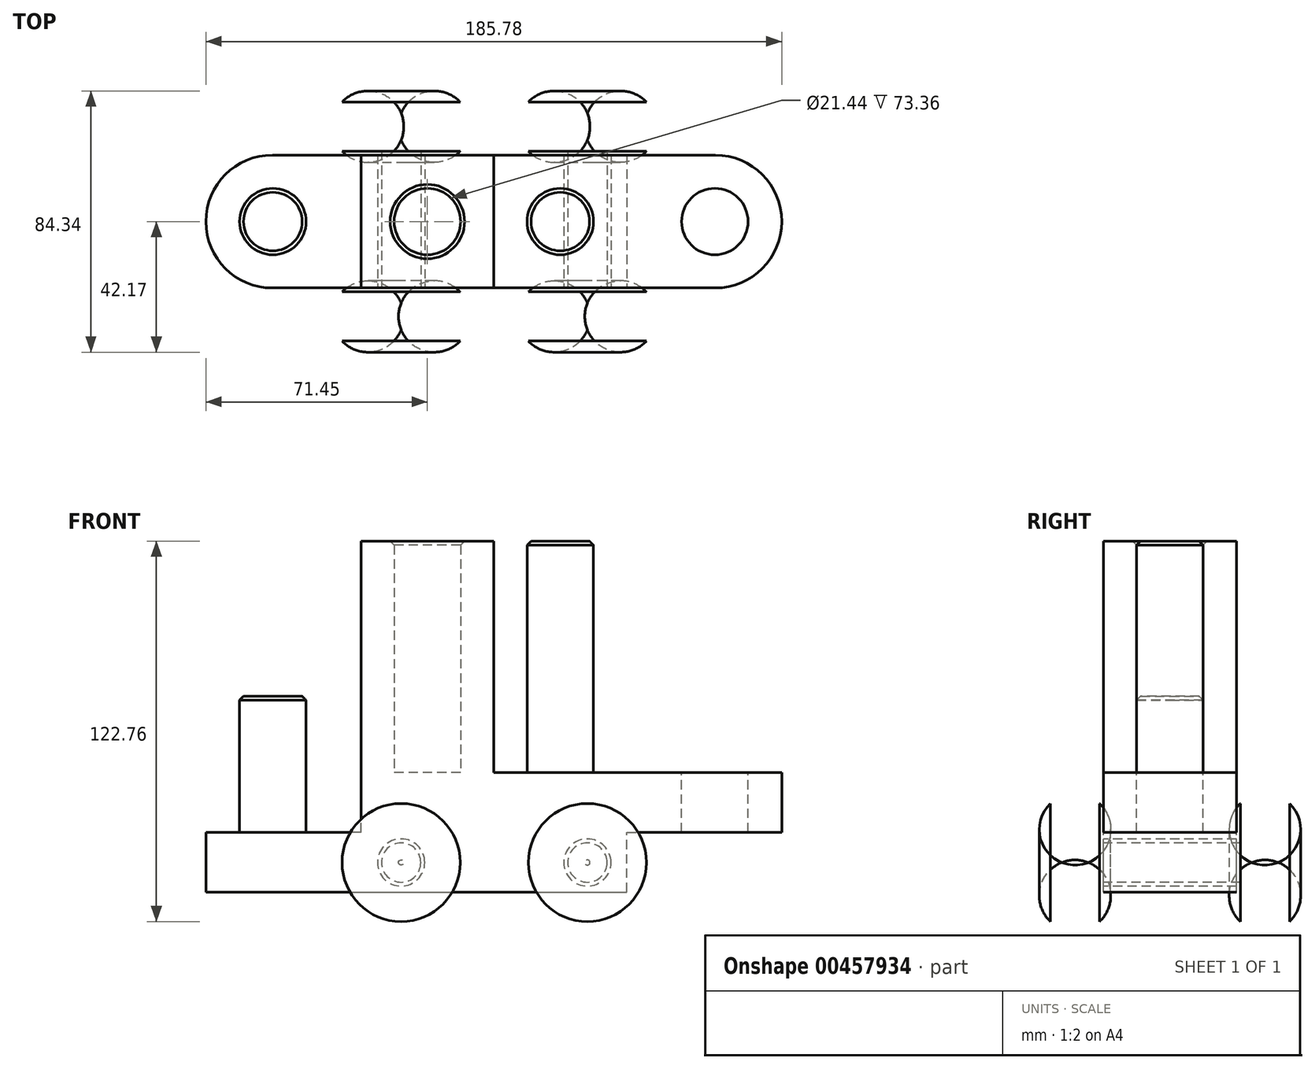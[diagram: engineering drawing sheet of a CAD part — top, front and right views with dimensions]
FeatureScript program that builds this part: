
annotation { "Feature Type Name" : "Feature", "Feature Type Description" : "" }
export const myFeature = defineFeature(function(context is Context, id is Id, definition is map)
    precondition{}
    {
        {
            var Q0;
            Q0=qCreatedBy(makeId("Top.planeOp"),FACE);
            var sketch = newSketch(context, id + "F0", { "sketchPlane" : qUnion([Q0])});
            skLineSegment(sketch, "E0.bottom", {"start": v(-42.88, 21.44) * mm, "end": v(42.88, 21.44) * mm});
            skLineSegment(sketch, "E0.top", {"start": v(-42.88, -21.44) * mm, "end": v(42.88, -21.44) * mm});
            skLineSegment(sketch, "E0.left", {"start": v(-42.88, 21.44) * mm, "end": v(-42.88, -21.44) * mm});
            skLineSegment(sketch, "E0.right", {"start": v(42.88, 21.44) * mm, "end": v(42.88, -21.44) * mm});
            skPoint(sketch, "E0.middle", {"position": v(0, 0) * mm});
            skLineSegment(sketch, "E1", {"start": v(-42.88, 0) * mm, "end": v(0, 0) * mm});
            skLineSegment(sketch, "E2", {"start": v(42.88, 0) * mm, "end": v(0, 0) * mm});
            skPoint(sketch, "E3", {"position": v(-21.44, 0) * mm});
            skPoint(sketch, "E4", {"position": v(21.44, 0) * mm});
            skCircle(sketch, "E5", {"center": v(-21.44, 0) * mm, "radius": 10.72 * mm});
            skCircle(sketch, "E6", {"center": v(21.44, 0) * mm, "radius": 10.72 * mm});
            skLineSegment(sketch, "E7", {"start": v(42.88, 21.44) * mm, "end": v(71.45, 21.44) * mm});
            skLineSegment(sketch, "E8", {"start": v(42.88, -21.44) * mm, "end": v(71.45, -21.44) * mm});
            skArc(sketch, "E9", {"start": v(71.45, -21.44) * mm, "mid": v(92.89, 0) * mm, "end": v(71.45, 21.44) * mm});
            skLineSegment(sketch, "E10", {"start": v(42.88, 0) * mm, "end": v(92.89, 0) * mm});
            skPoint(sketch, "E11", {"position": v(82.02, 0) * mm});
            skCircle(sketch, "E12", {"center": v(71.3, 0) * mm, "radius": 10.72 * mm});
            skLineSegment(sketch, "E13", {"start": v(0, 21.44) * mm, "end": v(0, -21.44) * mm});
            skLineSegment(sketch, "E14.MirrorCS", {"start": v(-42.88, 21.44) * mm, "end": v(-71.45, 21.44) * mm});
            skCircle(sketch, "E15.MirrorC", {"center": v(-71.3, 0) * mm, "radius": 10.72 * mm});
            skLineSegment(sketch, "E16.MirrorCS", {"start": v(-42.88, -21.44) * mm, "end": v(-71.45, -21.44) * mm});
            skPoint(sketch, "E17.MirrorP", {"position": v(-82.02, 0) * mm});
            skLineSegment(sketch, "E18.MirrorCS", {"start": v(-42.88, 0) * mm, "end": v(-92.89, 0) * mm});
            skArc(sketch, "E19.MirrorCS", {"start": v(-71.45, -21.44) * mm, "mid": v(-92.89, 0) * mm, "end": v(-71.45, 21.44) * mm});
            skSolve(sketch);
        }
        {
            var Q0;
            {var subQ6=sQuery(id+"F0.wireOp",EDGE,"E0.bottom");Q0=makeQuery(id+"F0.imprint","IMPRINT",FACE,{"disambiguationData":[TD([[makeQuery(id+"F0.imprint","IMPRINT",EDGE,{"derivedFrom":subQ6}),-1.0]])]});}
            var Q1;
            {var subQ0=sQuery(id+"F0.wireOp",EDGE,"E5");var subQ1=sQuery(id+"F0.wireOp",EDGE,"E1");var subQ2=makeQuery(id+"F0.imprint","INTERSECT",VERTEX,{"disambiguationData":[OD(0.0)],"derivedFrom":[subQ1,subQ0]});Q1=makeQuery(id+"F0.imprint","IMPRINT",FACE,{"disambiguationData":[TD([[makeQuery(id+"F0.imprint","IMPRINT",EDGE,{"disambiguationData":[TD([[subQ2,-1.0]])],"derivedFrom":subQ1}),1.0]])]});}
            var Q2;
            {var subQ0=sQuery(id+"F0.wireOp",EDGE,"E5");var subQ1=sQuery(id+"F0.wireOp",EDGE,"E1");var subQ2=makeQuery(id+"F0.imprint","INTERSECT",VERTEX,{"disambiguationData":[OD(0.0)],"derivedFrom":[subQ1,subQ0]});Q2=makeQuery(id+"F0.imprint","IMPRINT",FACE,{"disambiguationData":[TD([[makeQuery(id+"F0.imprint","IMPRINT",EDGE,{"disambiguationData":[TD([[subQ2,-1.0]])],"derivedFrom":subQ1}),-1.0]])]});}
            var Q3;
            {var subQ0=sQuery(id+"F0.wireOp",EDGE,"E6");var subQ1=sQuery(id+"F0.wireOp",EDGE,"E2");var subQ2=makeQuery(id+"F0.imprint","INTERSECT",VERTEX,{"disambiguationData":[OD(0.0)],"derivedFrom":[subQ1,subQ0]});Q3=makeQuery(id+"F0.imprint","IMPRINT",FACE,{"disambiguationData":[TD([[makeQuery(id+"F0.imprint","IMPRINT",EDGE,{"disambiguationData":[TD([[subQ2,-1.0]])],"derivedFrom":subQ1}),-1.0]])]});}
            var Q4;
            {var subQ0=sQuery(id+"F0.wireOp",EDGE,"E6");var subQ1=sQuery(id+"F0.wireOp",EDGE,"E2");var subQ2=makeQuery(id+"F0.imprint","INTERSECT",VERTEX,{"disambiguationData":[OD(0.0)],"derivedFrom":[subQ1,subQ0]});Q4=makeQuery(id+"F0.imprint","IMPRINT",FACE,{"disambiguationData":[TD([[makeQuery(id+"F0.imprint","IMPRINT",EDGE,{"disambiguationData":[TD([[subQ2,-1.0]])],"derivedFrom":subQ1}),1.0]])]});}
            var Q5;
            {var subQ1=sQuery(id+"F0.wireOp",EDGE,"E0.top");Q5=makeQuery(id+"F0.imprint","IMPRINT",FACE,{"disambiguationData":[TD([[makeQuery(id+"F0.imprint","IMPRINT",EDGE,{"derivedFrom":subQ1}),1.0]])]});}
            var Q6;
            {var subQ0=sQuery(id+"F0.wireOp",EDGE,"E1");var subQ1=sQuery(id+"F0.wireOp",EDGE,"E5");var subQ2=makeQuery(id+"F0.imprint","INTERSECT",VERTEX,{"disambiguationData":[OD(0.0)],"derivedFrom":[subQ1,subQ0]});Q6=makeQuery(id+"F0.imprint","IMPRINT",FACE,{"disambiguationData":[TD([[makeQuery(id+"F0.imprint","IMPRINT",EDGE,{"disambiguationData":[TD([[subQ2,-1.0]])],"derivedFrom":subQ1}),-1.0]])]});}
            var Q7;
            {var subQ0=sQuery(id+"F0.wireOp",EDGE,"E1");var subQ1=sQuery(id+"F0.wireOp",EDGE,"E5");var subQ2=makeQuery(id+"F0.imprint","INTERSECT",VERTEX,{"disambiguationData":[OD(0.0)],"derivedFrom":[subQ1,subQ0]});Q7=makeQuery(id+"F0.imprint","IMPRINT",FACE,{"disambiguationData":[TD([[makeQuery(id+"F0.imprint","IMPRINT",EDGE,{"disambiguationData":[TD([[subQ2,1.0]])],"derivedFrom":subQ1}),-1.0]])]});}
            extrude(context, id + "F1", {"entities" : qUnion([Q0, Q1, Q2, Q3, Q4, Q5, Q6, Q7]), "oppositeDirection" : true, "depth" : 38.6 * mm, "offsetDistance" : 25.4 * mm});
        }
        {
            var Q0;
            {var subQ0=sQuery(id+"F0.wireOp",EDGE,"E1");var subQ1=sQuery(id+"F0.wireOp",EDGE,"E5");var subQ2=makeQuery(id+"F0.imprint","INTERSECT",VERTEX,{"disambiguationData":[OD(0.0)],"derivedFrom":[subQ1,subQ0]});Q0=makeQuery(id+"F0.imprint","IMPRINT",FACE,{"disambiguationData":[TD([[makeQuery(id+"F0.imprint","IMPRINT",EDGE,{"disambiguationData":[TD([[subQ2,-1.0]])],"derivedFrom":subQ1}),-1.0]])]});}
            var Q1;
            {var subQ0=sQuery(id+"F0.wireOp",EDGE,"E1");var subQ1=sQuery(id+"F0.wireOp",EDGE,"E5");var subQ2=makeQuery(id+"F0.imprint","INTERSECT",VERTEX,{"disambiguationData":[OD(0.0)],"derivedFrom":[subQ1,subQ0]});Q1=makeQuery(id+"F0.imprint","IMPRINT",FACE,{"disambiguationData":[TD([[makeQuery(id+"F0.imprint","IMPRINT",EDGE,{"disambiguationData":[TD([[subQ2,1.0]])],"derivedFrom":subQ1}),-1.0]])]});}
            var Q2;
            {var subQ0=sQuery(id+"F0.wireOp",EDGE,"E6");var subQ1=sQuery(id+"F0.wireOp",EDGE,"E2");var subQ2=makeQuery(id+"F0.imprint","INTERSECT",VERTEX,{"disambiguationData":[OD(0.0)],"derivedFrom":[subQ1,subQ0]});Q2=makeQuery(id+"F0.imprint","IMPRINT",FACE,{"disambiguationData":[TD([[makeQuery(id+"F0.imprint","IMPRINT",EDGE,{"disambiguationData":[TD([[subQ2,-1.0]])],"derivedFrom":subQ1}),-1.0]])]});}
            var Q3;
            {var subQ0=sQuery(id+"F0.wireOp",EDGE,"E6");var subQ1=sQuery(id+"F0.wireOp",EDGE,"E2");var subQ2=makeQuery(id+"F0.imprint","INTERSECT",VERTEX,{"disambiguationData":[OD(0.0)],"derivedFrom":[subQ1,subQ0]});Q3=makeQuery(id+"F0.imprint","IMPRINT",FACE,{"disambiguationData":[TD([[makeQuery(id+"F0.imprint","IMPRINT",EDGE,{"disambiguationData":[TD([[subQ2,-1.0]])],"derivedFrom":subQ1}),1.0]])]});}
            extrude(context, id + "F2", {"entities" : qUnion([Q0, Q1, Q2, Q3]), "operationType" : NewBodyOperationType.ADD, "depth" : 74.63 * mm, "offsetDistance" : 25.4 * mm});
        }
        {
            var Q0;
            {var subQ5=sQuery(id+"F0.wireOp",EDGE,"E7");Q0=makeQuery(id+"F0.imprint","IMPRINT",FACE,{"disambiguationData":[TD([[makeQuery(id+"F0.imprint","IMPRINT",EDGE,{"derivedFrom":subQ5}),-1.0]])]});}
            var Q1;
            {var subQ1=sQuery(id+"F0.wireOp",EDGE,"E8");Q1=makeQuery(id+"F0.imprint","IMPRINT",FACE,{"disambiguationData":[TD([[makeQuery(id+"F0.imprint","IMPRINT",EDGE,{"derivedFrom":subQ1}),1.0]])]});}
            extrude(context, id + "F3", {"entities" : qUnion([Q0, Q1]), "operationType" : NewBodyOperationType.ADD, "oppositeDirection" : true, "depth" : 19.3 * mm, "offsetDistance" : 25.4 * mm});
        }
        {
            var Q0;
            {var subQ8=sQuery(id+"F0.wireOp",EDGE,"E14.MirrorCS");Q0=makeQuery(id+"F0.imprint","IMPRINT",FACE,{"disambiguationData":[TD([[makeQuery(id+"F0.imprint","IMPRINT",EDGE,{"derivedFrom":subQ8}),1.0]])]});}
            var Q1;
            {var subQ5=sQuery(id+"F0.wireOp",EDGE,"E16.MirrorCS");Q1=makeQuery(id+"F0.imprint","IMPRINT",FACE,{"disambiguationData":[TD([[makeQuery(id+"F0.imprint","IMPRINT",EDGE,{"derivedFrom":subQ5}),-1.0]])]});}
            var Q2;
            {var subQ0=sQuery(id+"F0.wireOp",EDGE,"E15.MirrorC");var subQ1=sQuery(id+"F0.wireOp",EDGE,"E18.MirrorCS");var subQ2=makeQuery(id+"F0.imprint","INTERSECT",VERTEX,{"disambiguationData":[OD(0.0)],"derivedFrom":[subQ1,subQ0]});Q2=makeQuery(id+"F0.imprint","IMPRINT",FACE,{"disambiguationData":[TD([[makeQuery(id+"F0.imprint","IMPRINT",EDGE,{"disambiguationData":[TD([[subQ2,-1.0]])],"derivedFrom":subQ1}),-1.0]])]});}
            var Q3;
            {var subQ0=sQuery(id+"F0.wireOp",EDGE,"E15.MirrorC");var subQ1=sQuery(id+"F0.wireOp",EDGE,"E18.MirrorCS");var subQ2=makeQuery(id+"F0.imprint","INTERSECT",VERTEX,{"disambiguationData":[OD(0.0)],"derivedFrom":[subQ1,subQ0]});Q3=makeQuery(id+"F0.imprint","IMPRINT",FACE,{"disambiguationData":[TD([[makeQuery(id+"F0.imprint","IMPRINT",EDGE,{"disambiguationData":[TD([[subQ2,-1.0]])],"derivedFrom":subQ1}),1.0]])]});}
            extrude(context, id + "F4", {"entities" : qUnion([Q0, Q1, Q2, Q3]), "operationType" : NewBodyOperationType.ADD, "oppositeDirection" : true, "depth" : 38.6 * mm, "offsetDistance" : 25.4 * mm});
        }
        {
            var Q0;
            {var subQ8=sQuery(id+"F0.wireOp",EDGE,"E14.MirrorCS");Q0=makeQuery(id+"F0.imprint","IMPRINT",FACE,{"disambiguationData":[TD([[makeQuery(id+"F0.imprint","IMPRINT",EDGE,{"derivedFrom":subQ8}),1.0]])]});}
            var Q1;
            {var subQ5=sQuery(id+"F0.wireOp",EDGE,"E16.MirrorCS");Q1=makeQuery(id+"F0.imprint","IMPRINT",FACE,{"disambiguationData":[TD([[makeQuery(id+"F0.imprint","IMPRINT",EDGE,{"derivedFrom":subQ5}),-1.0]])]});}
            extrude(context, id + "F5", {"entities" : qUnion([Q0, Q1]), "operationType" : NewBodyOperationType.REMOVE, "oppositeDirection" : true, "depth" : 19.3 * mm, "offsetDistance" : 25.4 * mm});
        }
        {
            var Q0;
            {var subQ0=sQuery(id+"F0.wireOp",EDGE,"E15.MirrorC");var subQ1=sQuery(id+"F0.wireOp",EDGE,"E18.MirrorCS");var subQ2=makeQuery(id+"F0.imprint","INTERSECT",VERTEX,{"disambiguationData":[OD(0.0)],"derivedFrom":[subQ1,subQ0]});Q0=makeQuery(id+"F0.imprint","IMPRINT",FACE,{"disambiguationData":[TD([[makeQuery(id+"F0.imprint","IMPRINT",EDGE,{"disambiguationData":[TD([[subQ2,-1.0]])],"derivedFrom":subQ1}),-1.0]])]});}
            var Q1;
            {var subQ0=sQuery(id+"F0.wireOp",EDGE,"E15.MirrorC");var subQ1=sQuery(id+"F0.wireOp",EDGE,"E18.MirrorCS");var subQ2=makeQuery(id+"F0.imprint","INTERSECT",VERTEX,{"disambiguationData":[OD(0.0)],"derivedFrom":[subQ1,subQ0]});Q1=makeQuery(id+"F0.imprint","IMPRINT",FACE,{"disambiguationData":[TD([[makeQuery(id+"F0.imprint","IMPRINT",EDGE,{"disambiguationData":[TD([[subQ2,-1.0]])],"derivedFrom":subQ1}),1.0]])]});}
            extrude(context, id + "F6", {"entities" : qUnion([Q0, Q1]), "operationType" : NewBodyOperationType.ADD, "depth" : 24.59 * mm, "offsetDistance" : 25.4 * mm});
        }
        {
            var Q0;
            Q0=makeQuery(id+"F2.opExtrude","CAP_EDGE",EDGE,{"disambiguationData":[OSD([sQuery(id+"F0.wireOp",EDGE,"E5")])],"isStart":false});
            chamfer(context, id + "F7", {"entities" : qUnion([Q0]), "width" : 1.27 * mm, "tangentPropagation" : true});
        }
        {
            var Q0;
            Q0=makeQuery(id+"F2.opExtrude","CAP_EDGE",EDGE,{"disambiguationData":[OSD([sQuery(id+"F0.wireOp",EDGE,"E6")])],"isStart":false});
            chamfer(context, id + "F8", {"entities" : qUnion([Q0]), "width" : 1.27 * mm, "tangentPropagation" : true});
        }
        {
            var Q0;
            Q0=makeQuery(id+"F6.opExtrude","CAP_EDGE",EDGE,{"disambiguationData":[OSD([sQuery(id+"F0.wireOp",EDGE,"E15.MirrorC")])],"isStart":false});
            chamfer(context, id + "F9", {"entities" : qUnion([Q0]), "width" : 1.27 * mm, "tangentPropagation" : true});
        }
        {
            var Q0;
            Q0=makeQuery(id+"F4.boolean.opBoolean","MERGE",FACE,{"derivedFrom":[makeQuery(id+"F3.boolean.opBoolean","MERGE",FACE,{"derivedFrom":[makeQuery(id+"F1.opExtrude","SWEPT_FACE",FACE,{"disambiguationData":[OSD([sQuery(id+"F0.wireOp",EDGE,"E0.top")])]}),makeQuery(id+"F3.opExtrude","SWEPT_FACE",FACE,{"disambiguationData":[OSD([sQuery(id+"F0.wireOp",EDGE,"E8")])]})]}),makeQuery(id+"F4.opExtrude","SWEPT_FACE",FACE,{"disambiguationData":[OSD([sQuery(id+"F0.wireOp",EDGE,"E16.MirrorCS")])]})]});
            var sketch = newSketch(context, id + "F10", { "sketchPlane" : qUnion([Q0])});
            skPoint(sketch, "E20", {"position": v(42.88, -29.08) * mm});
            skLineSegment(sketch, "E21", {"start": v(42.88, -29.08) * mm, "end": v(30.18, -29.08) * mm});
            skCircle(sketch, "E22", {"center": v(30.18, -29.08) * mm, "radius": 6.35 * mm});
            skCircle(sketch, "E23", {"center": v(30.18, -29.08) * mm, "radius": 7.62 * mm});
            skLineSegment(sketch, "E24", {"start": v(30.18, -29.08) * mm, "end": v(-29.91, -29.08) * mm});
            skCircle(sketch, "E25", {"center": v(-29.91, -29.08) * mm, "radius": 6.35 * mm});
            skCircle(sketch, "E26", {"center": v(-29.91, -29.08) * mm, "radius": 7.62 * mm});
            skSolve(sketch);
        }
        {
            var Q0;
            {var subQ0=sQuery(id+"F10.wireOp",EDGE,"E23");var subQ1=sQuery(id+"F10.wireOp",EDGE,"E21");var subQ2=makeQuery(id+"F10.imprint","INTERSECT",VERTEX,{"derivedFrom":[subQ1,subQ0]});Q0=makeQuery(id+"F10.imprint","IMPRINT",FACE,{"disambiguationData":[TD([[makeQuery(id+"F10.imprint","IMPRINT",EDGE,{"disambiguationData":[TD([[subQ2,-1.0]])],"derivedFrom":subQ1}),-1.0]])]});}
            var Q1;
            {var subQ0=sQuery(id+"F10.wireOp",EDGE,"E23");var subQ1=sQuery(id+"F10.wireOp",EDGE,"E21");var subQ2=makeQuery(id+"F10.imprint","INTERSECT",VERTEX,{"derivedFrom":[subQ1,subQ0]});Q1=makeQuery(id+"F10.imprint","IMPRINT",FACE,{"disambiguationData":[TD([[makeQuery(id+"F10.imprint","IMPRINT",EDGE,{"disambiguationData":[TD([[subQ2,-1.0]])],"derivedFrom":subQ1}),1.0]])]});}
            var Q2;
            Q2=makeQuery(id+"F10.imprint","IMPRINT",FACE,{"disambiguationData":[TD([[makeQuery(id+"F10.imprint","IMPRINT",EDGE,{"derivedFrom":sQuery(id+"F10.wireOp",EDGE,"E25")}),-1.0]])]});
            var Q3;
            Q3=makeQuery(id+"F4.boolean.opBoolean","MERGE",FACE,{"derivedFrom":[makeQuery(id+"F3.boolean.opBoolean","MERGE",FACE,{"derivedFrom":[makeQuery(id+"F1.opExtrude","SWEPT_FACE",FACE,{"disambiguationData":[OSD([sQuery(id+"F0.wireOp",EDGE,"E0.bottom")])]}),makeQuery(id+"F3.opExtrude","SWEPT_FACE",FACE,{"disambiguationData":[OSD([sQuery(id+"F0.wireOp",EDGE,"E7")])]})]}),makeQuery(id+"F4.opExtrude","SWEPT_FACE",FACE,{"disambiguationData":[OSD([sQuery(id+"F0.wireOp",EDGE,"E14.MirrorCS")])]})]});
            extrude(context, id + "F11", {"entities" : qUnion([Q0, Q1, Q2]), "operationType" : NewBodyOperationType.REMOVE, "endBound" : BoundingType.UP_TO_SURFACE, "oppositeDirection" : true, "depth" : 25.4 * mm, "endBoundEntityFace" : qUnion([Q3]), "offsetDistance" : 25.4 * mm});
        }
        {
            var Q0;
            Q0=makeQuery(id+"F11.boolean.opBoolean","SPLIT",FACE,{"disambiguationData":[TD([makeQuery(id+"F11.opExtrude","SWEPT_FACE",FACE,{"disambiguationData":[OSD([sQuery(id+"F10.wireOp",EDGE,"E22")])]})])],"derivedFrom":makeQuery(id+"F4.boolean.opBoolean","MERGE",FACE,{"derivedFrom":[makeQuery(id+"F3.boolean.opBoolean","MERGE",FACE,{"derivedFrom":[makeQuery(id+"F1.opExtrude","SWEPT_FACE",FACE,{"disambiguationData":[OSD([sQuery(id+"F0.wireOp",EDGE,"E0.top")])]}),makeQuery(id+"F3.opExtrude","SWEPT_FACE",FACE,{"disambiguationData":[OSD([sQuery(id+"F0.wireOp",EDGE,"E8")])]})]}),makeQuery(id+"F4.opExtrude","SWEPT_FACE",FACE,{"disambiguationData":[OSD([sQuery(id+"F0.wireOp",EDGE,"E16.MirrorCS")])]})]})});
            var Q1;
            Q1=makeQuery(id+"F11.boolean.opBoolean","SPLIT",FACE,{"disambiguationData":[TD([makeQuery(id+"F11.opExtrude","SWEPT_FACE",FACE,{"disambiguationData":[OSD([sQuery(id+"F10.wireOp",EDGE,"E25")])]})])],"derivedFrom":makeQuery(id+"F4.boolean.opBoolean","MERGE",FACE,{"derivedFrom":[makeQuery(id+"F3.boolean.opBoolean","MERGE",FACE,{"derivedFrom":[makeQuery(id+"F1.opExtrude","SWEPT_FACE",FACE,{"disambiguationData":[OSD([sQuery(id+"F0.wireOp",EDGE,"E0.top")])]}),makeQuery(id+"F3.opExtrude","SWEPT_FACE",FACE,{"disambiguationData":[OSD([sQuery(id+"F0.wireOp",EDGE,"E8")])]})]}),makeQuery(id+"F4.opExtrude","SWEPT_FACE",FACE,{"disambiguationData":[OSD([sQuery(id+"F0.wireOp",EDGE,"E16.MirrorCS")])]})]})});
            extrude(context, id + "F12", {"entities" : qUnion([Q0, Q1]), "operationType" : NewBodyOperationType.ADD, "depth" : 1.27 * mm, "offsetDistance" : 25.4 * mm});
        }
        {
            var Q0;
            Q0=makeQuery(id+"F11.boolean.opBoolean","SPLIT",FACE,{"disambiguationData":[TD([makeQuery(id+"F11.opExtrude","SWEPT_FACE",FACE,{"disambiguationData":[OSD([sQuery(id+"F10.wireOp",EDGE,"E25")])]})])],"derivedFrom":makeQuery(id+"F4.boolean.opBoolean","MERGE",FACE,{"derivedFrom":[makeQuery(id+"F3.boolean.opBoolean","MERGE",FACE,{"derivedFrom":[makeQuery(id+"F1.opExtrude","SWEPT_FACE",FACE,{"disambiguationData":[OSD([sQuery(id+"F0.wireOp",EDGE,"E0.bottom")])]}),makeQuery(id+"F3.opExtrude","SWEPT_FACE",FACE,{"disambiguationData":[OSD([sQuery(id+"F0.wireOp",EDGE,"E7")])]})]}),makeQuery(id+"F4.opExtrude","SWEPT_FACE",FACE,{"disambiguationData":[OSD([sQuery(id+"F0.wireOp",EDGE,"E14.MirrorCS")])]})]})});
            var Q1;
            Q1=makeQuery(id+"F11.boolean.opBoolean","SPLIT",FACE,{"disambiguationData":[TD([makeQuery(id+"F11.opExtrude","SWEPT_FACE",FACE,{"disambiguationData":[OSD([sQuery(id+"F10.wireOp",EDGE,"E22")])]})])],"derivedFrom":makeQuery(id+"F4.boolean.opBoolean","MERGE",FACE,{"derivedFrom":[makeQuery(id+"F3.boolean.opBoolean","MERGE",FACE,{"derivedFrom":[makeQuery(id+"F1.opExtrude","SWEPT_FACE",FACE,{"disambiguationData":[OSD([sQuery(id+"F0.wireOp",EDGE,"E0.bottom")])]}),makeQuery(id+"F3.opExtrude","SWEPT_FACE",FACE,{"disambiguationData":[OSD([sQuery(id+"F0.wireOp",EDGE,"E7")])]})]}),makeQuery(id+"F4.opExtrude","SWEPT_FACE",FACE,{"disambiguationData":[OSD([sQuery(id+"F0.wireOp",EDGE,"E14.MirrorCS")])]})]})});
            extrude(context, id + "F13", {"entities" : qUnion([Q0, Q1]), "operationType" : NewBodyOperationType.ADD, "depth" : 1.27 * mm, "offsetDistance" : 25.4 * mm});
        }
        {
            var Q0;
            Q0=sQuery(id+"F10.wireOp",EDGE,"E24");
            cPlane(context, id + "F14", {"entities" : qUnion([Q0]), "cplaneType" : CPlaneType.LINE_ANGLE, "offset" : 25.4 * mm, "angle" : 90 * degree, "width" : 152.4 * mm, "height" : 152.4 * mm});
        }
        {
            var Q0;
            Q0=qCreatedBy(id+"F14.planeOp",FACE);
            var sketch = newSketch(context, id + "F15", { "sketchPlane" : qUnion([Q0])});
            skLineSegment(sketch, "E27.0", {"start": v(-23.56, -22.7) * mm, "end": v(-36.26, -22.7) * mm});
            skLineSegment(sketch, "E28", {"start": v(-29.91, -22.7) * mm, "end": v(-29.91, -38.58) * mm});
            skLineSegment(sketch, "E29", {"start": v(-29.91, -22.7) * mm, "end": v(-10.86, -22.7) * mm});
            skLineSegment(sketch, "E30", {"start": v(-29.91, -38.58) * mm, "end": v(-10.86, -38.58) * mm});
            skArc(sketch, "E31", {"start": v(-10.86, -38.58) * mm, "mid": v(-7.69, -30.65) * mm, "end": v(-10.86, -22.7) * mm});
            skLineSegment(sketch, "E32.0", {"start": v(36.53, -22.7) * mm, "end": v(23.83, -22.7) * mm});
            skPoint(sketch, "E33", {"position": v(30.18, -22.7) * mm});
            skLineSegment(sketch, "E34", {"start": v(30.18, -22.7) * mm, "end": v(30.18, -38.58) * mm});
            skLineSegment(sketch, "E35", {"start": v(30.18, -22.7) * mm, "end": v(49.23, -22.7) * mm});
            skLineSegment(sketch, "E36", {"start": v(30.18, -38.58) * mm, "end": v(49.23, -38.58) * mm});
            skArc(sketch, "E37", {"start": v(49.23, -38.58) * mm, "mid": v(52.4, -30.65) * mm, "end": v(49.23, -22.7) * mm});
            skSolve(sketch);
        }
        {
            var Q0;
            {var subQ0=sQuery(id+"F15.wireOp",EDGE,"E28");Q0=makeQuery(id+"F15.imprint","IMPRINT",FACE,{"disambiguationData":[TD([[makeQuery(id+"F15.imprint","IMPRINT",EDGE,{"derivedFrom":subQ0}),1.0]])]});}
            var Q1;
            Q1=sQuery(id+"F15.wireOp",EDGE,"E28");
            revolve(context, id + "F16", {"entities" : qUnion([Q0]), "axis" : qUnion([Q1]), "revolveType" : RevolveType.FULL});
        }
        {
            var Q0;
            {var subQ3=sQuery(id+"F15.wireOp",EDGE,"E34");Q0=makeQuery(id+"F15.imprint","IMPRINT",FACE,{"disambiguationData":[TD([[makeQuery(id+"F15.imprint","IMPRINT",EDGE,{"derivedFrom":subQ3}),1.0]])]});}
            var Q1;
            Q1=sQuery(id+"F15.wireOp",EDGE,"E34");
            revolve(context, id + "F17", {"entities" : qUnion([Q0]), "axis" : qUnion([Q1]), "revolveType" : RevolveType.FULL});
        }
        {
            var Q0;
            Q0=makeQuery(id+"F16.opRevolve","SWEPT_BODY",BODY,{"disambiguationData":[OSD([sQuery(id+"F15.wireOp",EDGE,"E28"),sQuery(id+"F15.wireOp",EDGE,"E29"),sQuery(id+"F15.wireOp",EDGE,"E30"),sQuery(id+"F15.wireOp",EDGE,"E31")])]});
            var Q1;
            Q1=makeQuery(id+"F17.opRevolve","SWEPT_BODY",BODY,{"disambiguationData":[OSD([sQuery(id+"F15.wireOp",EDGE,"E34"),sQuery(id+"F15.wireOp",EDGE,"E35"),sQuery(id+"F15.wireOp",EDGE,"E36"),sQuery(id+"F15.wireOp",EDGE,"E37")])]});
            var Q2;
            Q2=qCreatedBy(makeId("Front.planeOp"),FACE);
            mirror(context, id + "F18", {"entities" : qUnion([Q0, Q1]), "mirrorPlane" : qUnion([Q2])});
        }
    });
